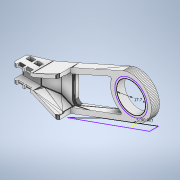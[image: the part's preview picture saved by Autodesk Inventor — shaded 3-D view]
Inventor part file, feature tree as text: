
AUTODESK INVENTOR PART (.ipt)
format: ipt  version: 2020 (Build 240168000, 168)  size: 4,963,840 bytes
history: native  units: in
note: dims shown in document units (in); Inventor stores cm internally (conversion verified against a paired STEP export)
features: sketch x3, extrude x3, other x2
ambient origin geometry x8: Origin, YZ Plane, XZ Plane, XY Plane, X Axis, Y Axis, Z Axis, Center Point
bodies: Solid1 (feature_tree)
feature tree (8):
  other  "Wire_Strain_Relief_Bracket_Base"
  other  "MeshFeature1"
  sketch  "Sketch1"  dims[d0=0.1969in d1=90.0deg]
  extrude  "Extrusion1"  TaperAngle=90.0deg  [1 undecoded]
  sketch  "Sketch3"  dims[d5=0.315in d6=0.0in d7=0.3937in d8=0.0in]
  extrude  "Extrusion2"  Depth=0.6969in
  extrude  "Extrusion3"  Depth=0.3937in TaperAngle=0.0deg
  sketch  "Sketch2"  dims[d2=0.315in d3=0.0in d4=0.6969in]
note: 1 required parameter value undecoded (feature->parameter linkage not recoverable at this tier; creation-order binding heuristic only, values carry confidence <= 0.55)
